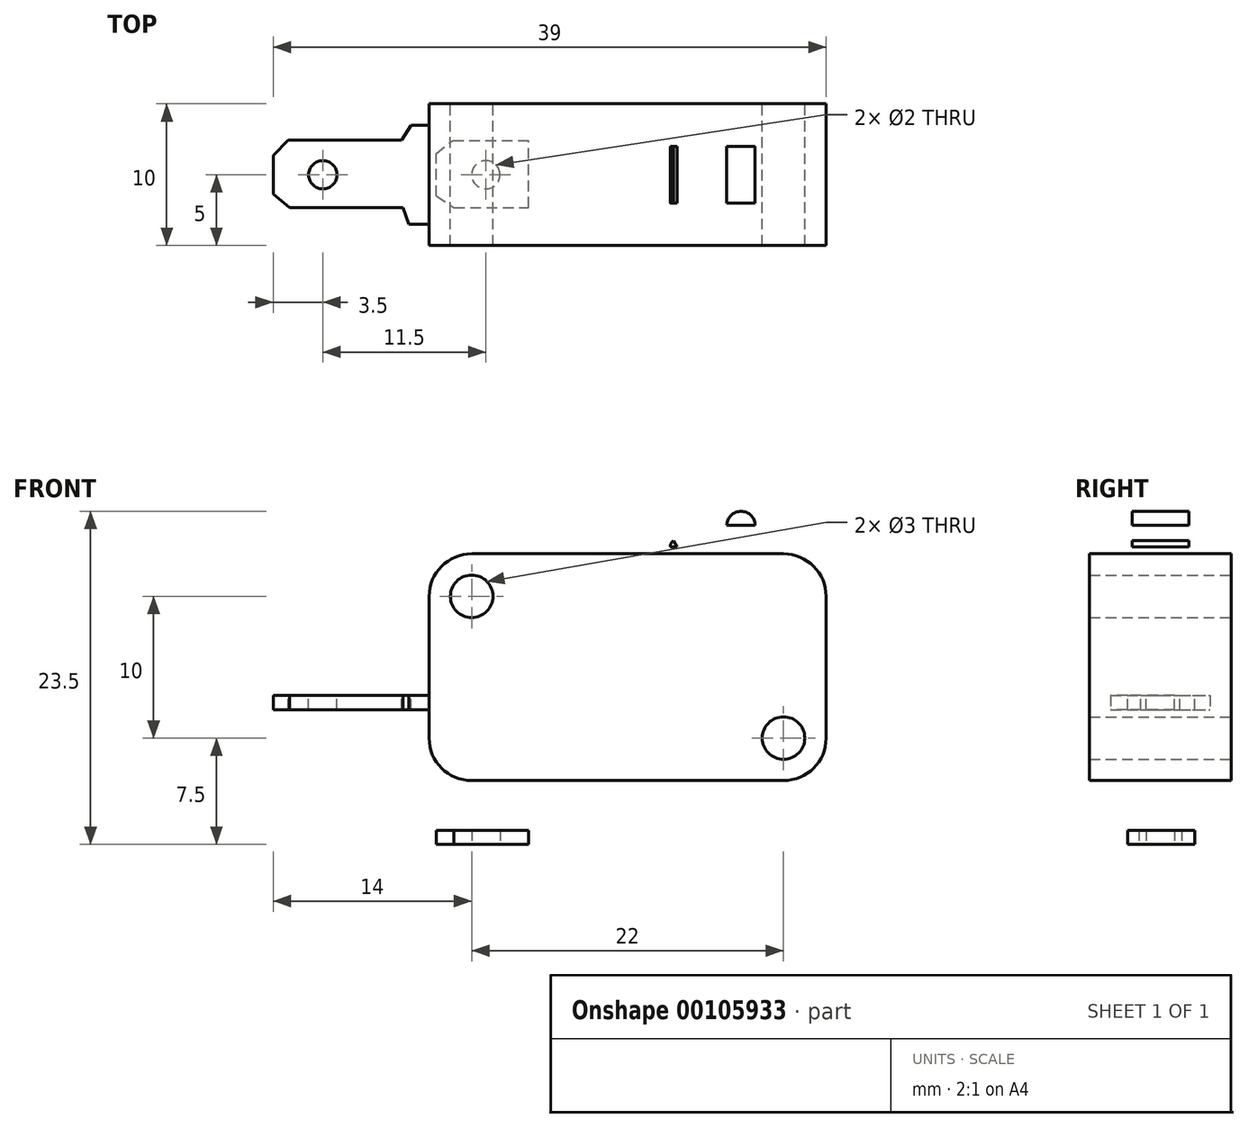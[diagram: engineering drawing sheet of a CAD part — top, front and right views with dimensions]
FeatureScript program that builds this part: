
annotation { "Feature Type Name" : "Feature", "Feature Type Description" : "" }
export const myFeature = defineFeature(function(context is Context, id is Id, definition is map)
    precondition{}
    {
        {
            var Q0;
            Q0=qCreatedBy(makeId("Front.planeOp"),FACE);
            var sketch = newSketch(context, id + "F0", { "sketchPlane" : qUnion([Q0])});
            skLineSegment(sketch, "E0.bottom", {"start": v(11, 8) * mm, "end": v(-11, 8) * mm});
            skLineSegment(sketch, "E0.top", {"start": v(11, -8) * mm, "end": v(-11, -8) * mm});
            skLineSegment(sketch, "E0.left", {"start": v(14, 5) * mm, "end": v(14, -5) * mm});
            skLineSegment(sketch, "E0.right", {"start": v(-14, 5) * mm, "end": v(-14, -5) * mm});
            skPoint(sketch, "E0.middle", {"position": v(0, 0) * mm});
            skPoint(sketch, "E1.visualSharp", {"position": v(-14, -8) * mm});
            skArc(sketch, "E1.filletArc", {"start": v(-14, -5) * mm, "mid": v(-13.12, -7.12) * mm, "end": v(-11, -8) * mm});
            skPoint(sketch, "E2.visualSharp", {"position": v(-14, 8) * mm});
            skArc(sketch, "E2.filletArc", {"start": v(-11, 8) * mm, "mid": v(-13.12, 7.12) * mm, "end": v(-14, 5) * mm});
            skPoint(sketch, "E3.visualSharp", {"position": v(14, 8) * mm});
            skArc(sketch, "E3.filletArc", {"start": v(14, 5) * mm, "mid": v(13.12, 7.12) * mm, "end": v(11, 8) * mm});
            skPoint(sketch, "E4.visualSharp", {"position": v(14, -8) * mm});
            skArc(sketch, "E4.filletArc", {"start": v(11, -8) * mm, "mid": v(13.12, -7.12) * mm, "end": v(14, -5) * mm});
            skCircle(sketch, "E5", {"center": v(-11, 5) * mm, "radius": 1.5 * mm});
            skCircle(sketch, "E6", {"center": v(11, -5) * mm, "radius": 1.5 * mm});
            skLineSegment(sketch, "E7.bottom", {"start": v(7, 8) * mm, "end": v(9, 8) * mm});
            skLineSegment(sketch, "E7.top", {"start": v(7, 10) * mm, "end": v(9, 10) * mm});
            skLineSegment(sketch, "E7.left", {"start": v(7, 8) * mm, "end": v(7, 10) * mm});
            skLineSegment(sketch, "E7.right", {"start": v(9, 8) * mm, "end": v(9, 10) * mm});
            skArc(sketch, "E8", {"start": v(9, 10) * mm, "mid": v(8, 11) * mm, "end": v(7, 10) * mm});
            skLineSegment(sketch, "E9.bottom", {"start": v(3, 8) * mm, "end": v(3.5, 8) * mm});
            skLineSegment(sketch, "E9.top", {"start": v(3, 8.5) * mm, "end": v(3.5, 8.5) * mm});
            skLineSegment(sketch, "E9.left", {"start": v(3, 8) * mm, "end": v(3, 8.5) * mm});
            skLineSegment(sketch, "E9.right", {"start": v(3.5, 8) * mm, "end": v(3.5, 8.46) * mm});
            skLineSegment(sketch, "E10", {"start": v(3.53, 8.52) * mm, "end": v(46.53, 33.96) * mm});
            skLineSegment(sketch, "E11", {"start": v(3.5, 8.5) * mm, "end": v(3.25, 8.93) * mm});
            skLineSegment(sketch, "E12", {"start": v(3.25, 8.93) * mm, "end": v(46.28, 34.39) * mm});
            skLineSegment(sketch, "E13", {"start": v(46.28, 34.39) * mm, "end": v(46.53, 33.96) * mm});
            skArc(sketch, "E14", {"start": v(3.25, 8.93) * mm, "mid": v(3.07, 8.75) * mm, "end": v(3, 8.5) * mm});
            skArc(sketch, "E15.filletArc", {"start": v(3.53, 8.52) * mm, "mid": v(3.5, 8.5) * mm, "end": v(3.5, 8.46) * mm});
            skLineSegment(sketch, "E16.bottom", {"start": v(-14, -2) * mm, "end": v(-25, -2) * mm});
            skLineSegment(sketch, "E16.top", {"start": v(-14, -3) * mm, "end": v(-25, -3) * mm});
            skLineSegment(sketch, "E16.left", {"start": v(-14, -2) * mm, "end": v(-14, -3) * mm});
            skLineSegment(sketch, "E16.right", {"start": v(-25, -2) * mm, "end": v(-25, -3) * mm});
            skLineSegment(sketch, "E17.bottom", {"start": v(-7, -8) * mm, "end": v(-1, -8) * mm});
            skLineSegment(sketch, "E17.top", {"start": v(-7, -12.5) * mm, "end": v(-3.5, -12.5) * mm});
            skLineSegment(sketch, "E17.left", {"start": v(-7, -8) * mm, "end": v(-7, -12.5) * mm});
            skLineSegment(sketch, "E17.right", {"start": v(-1, -8) * mm, "end": v(-1, -10) * mm});
            skLineSegment(sketch, "E18.bottom", {"start": v(-7, -12.5) * mm, "end": v(-13.5, -12.5) * mm});
            skLineSegment(sketch, "E18.top", {"start": v(-7, -11.5) * mm, "end": v(-13.5, -11.5) * mm});
            skLineSegment(sketch, "E18.left", {"start": v(-7, -12.5) * mm, "end": v(-7, -11.5) * mm});
            skLineSegment(sketch, "E18.right", {"start": v(-13.5, -12.5) * mm, "end": v(-13.5, -11.5) * mm});
            skLineSegment(sketch, "E19.bottom", {"start": v(-7, -11.5) * mm, "end": v(-3.5, -11.5) * mm});
            skLineSegment(sketch, "E19.top", {"start": v(-7, -8) * mm, "end": v(-2, -8) * mm});
            skLineSegment(sketch, "E19.left", {"start": v(-7, -11.5) * mm, "end": v(-7, -8) * mm});
            skLineSegment(sketch, "E19.right", {"start": v(-2, -10) * mm, "end": v(-2, -8) * mm});
            skPoint(sketch, "E20.visualSharp", {"position": v(-2, -11.5) * mm});
            skArc(sketch, "E20.filletArc", {"start": v(-3.5, -11.5) * mm, "mid": v(-2.44, -11.06) * mm, "end": v(-2, -10) * mm});
            skPoint(sketch, "E21.visualSharp", {"position": v(-1, -12.5) * mm});
            skArc(sketch, "E21.filletArc", {"start": v(-3.5, -12.5) * mm, "mid": v(-1.73, -11.77) * mm, "end": v(-1, -10) * mm});
            skSolve(sketch);
        }
        {
            var Q0;
            Q0=makeQuery(id+"F0.imprint","IMPRINT",FACE,{"disambiguationData":[TD([[makeQuery(id+"F0.imprint","IMPRINT",EDGE,{"derivedFrom":sQuery(id+"F0.wireOp",EDGE,"E0.left")}),-1.0]])]});
            extrude(context, id + "F1", {"entities" : qUnion([Q0]), "endBound" : BoundingType.SYMMETRIC, "depth" : 10 * mm});
        }
        {
            var Q0;
            Q0=makeQuery(id+"F0.imprint","IMPRINT",FACE,{"disambiguationData":[TD([[makeQuery(id+"F0.imprint","IMPRINT",EDGE,{"derivedFrom":sQuery(id+"F0.wireOp",EDGE,"E18.bottom")}),-1.0]])]});
            var Q1;
            Q1=makeQuery(id+"F0.imprint","IMPRINT",FACE,{"disambiguationData":[TD([[makeQuery(id+"F0.imprint","IMPRINT",EDGE,{"derivedFrom":sQuery(id+"F0.wireOp",EDGE,"E17.bottom")}),-1.0]])]});
            var Q2;
            Q2=makeQuery(id+"F0.imprint","IMPRINT",FACE,{"disambiguationData":[TD([[makeQuery(id+"F0.imprint","IMPRINT",EDGE,{"derivedFrom":sQuery(id+"F0.wireOp",EDGE,"E16.bottom")}),1.0]])]});
            extrude(context, id + "F2", {"entities" : qUnion([Q0, Q1, Q2]), "endBound" : BoundingType.SYMMETRIC, "depth" : 7 * mm});
        }
        {
            var Q0;
            Q0=makeQuery(id+"F0.imprint","IMPRINT",FACE,{"disambiguationData":[TD([[makeQuery(id+"F0.imprint","IMPRINT",EDGE,{"derivedFrom":sQuery(id+"F0.wireOp",EDGE,"E7.bottom")}),1.0]])]});
            var Q1;
            {var subQ0=sQuery(id+"F0.wireOp",EDGE,"E7.top");Q1=makeQuery(id+"F0.imprint","IMPRINT",FACE,{"disambiguationData":[TD([[makeQuery(id+"F0.imprint","IMPRINT",EDGE,{"derivedFrom":subQ0}),1.0]])]});}
            var Q2;
            Q2=makeQuery(id+"F0.imprint","IMPRINT",FACE,{"disambiguationData":[TD([[makeQuery(id+"F0.imprint","IMPRINT",EDGE,{"derivedFrom":sQuery(id+"F0.wireOp",EDGE,"E9.bottom")}),1.0]])]});
            var Q3;
            Q3=makeQuery(id+"F0.imprint","IMPRINT",FACE,{"disambiguationData":[TD([[makeQuery(id+"F0.imprint","IMPRINT",EDGE,{"derivedFrom":sQuery(id+"F0.wireOp",EDGE,"E9.top")}),1.0]])]});
            extrude(context, id + "F3", {"entities" : qUnion([Q0, Q1, Q2, Q3]), "endBound" : BoundingType.SYMMETRIC, "depth" : 4 * mm});
        }
        {
            var Q0;
            Q0=makeQuery(id+"F2.opExtrude","SWEPT_FACE",FACE,{"disambiguationData":[OSD([sQuery(id+"F0.wireOp",EDGE,"E17.top"),sQuery(id+"F0.wireOp",EDGE,"E18.bottom")])]});
            var sketch = newSketch(context, id + "F4", { "sketchPlane" : qUnion([Q0])});
            skCircle(sketch, "E22", {"center": v(-10, 0) * mm, "radius": 1 * mm});
            skLineSegment(sketch, "E23", {"start": v(-13.5, 0) * mm, "end": v(-11, 0) * mm});
            skLineSegment(sketch, "E24", {"start": v(-13.5, -1.5) * mm, "end": v(-13.5, 1.5) * mm});
            skLineSegment(sketch, "E25", {"start": v(-13.5, -1.5) * mm, "end": v(-12.32, -2.43) * mm});
            skLineSegment(sketch, "E26", {"start": v(-13.5, 1.5) * mm, "end": v(-12.24, 2.32) * mm});
            skLineSegment(sketch, "E27", {"start": v(-12.24, 2.32) * mm, "end": v(-5.4, 2.32) * mm});
            skLineSegment(sketch, "E28", {"start": v(-5.4, 2.32) * mm, "end": v(-4.85, 3.5) * mm});
            skLineSegment(sketch, "E29", {"start": v(-12.32, -2.43) * mm, "end": v(-5.47, -2.43) * mm});
            skLineSegment(sketch, "E30", {"start": v(-5.47, -2.43) * mm, "end": v(-4.74, -3.5) * mm});
            skSolve(sketch);
        }
        {
            var Q0;
            {var subQ5=sQuery(id+"F4.wireOp",EDGE,"E26");Q0=makeQuery(id+"F4.imprint","IMPRINT",FACE,{"disambiguationData":[TD([[makeQuery(id+"F4.imprint","IMPRINT",EDGE,{"derivedFrom":subQ5}),1.0]])]});}
            var Q1;
            Q1=makeQuery(id+"F4.imprint","IMPRINT",FACE,{"disambiguationData":[TD([[makeQuery(id+"F4.imprint","IMPRINT",EDGE,{"derivedFrom":sQuery(id+"F4.wireOp",EDGE,"E22")}),1.0]])]});
            var Q2;
            {var subQ4=sQuery(id+"F4.wireOp",EDGE,"E25");Q2=makeQuery(id+"F4.imprint","IMPRINT",FACE,{"disambiguationData":[TD([[makeQuery(id+"F4.imprint","IMPRINT",EDGE,{"derivedFrom":subQ4}),-1.0]])]});}
            extrude(context, id + "F5", {"entities" : qUnion([Q0, Q1, Q2]), "operationType" : NewBodyOperationType.REMOVE, "oppositeDirection" : true, "depth" : 1 * mm});
        }
        {
            var Q0;
            Q0=makeQuery(id+"F2.opExtrude","SWEPT_FACE",FACE,{"disambiguationData":[OSD([sQuery(id+"F0.wireOp",EDGE,"E16.bottom")])]});
            var sketch = newSketch(context, id + "F6", { "sketchPlane" : qUnion([Q0])});
            skLineSegment(sketch, "E31", {"start": v(-25, 1.38) * mm, "end": v(-25, -1.38) * mm});
            skLineSegment(sketch, "E32", {"start": v(-25, 1.37) * mm, "end": v(-23.94, 2.43) * mm});
            skLineSegment(sketch, "E33", {"start": v(-23.94, 2.43) * mm, "end": v(-15.94, 2.43) * mm});
            skLineSegment(sketch, "E34", {"start": v(-15.94, 2.43) * mm, "end": v(-15.29, 3.5) * mm});
            skLineSegment(sketch, "E35", {"start": v(-25, -1.37) * mm, "end": v(-23.83, -2.32) * mm});
            skLineSegment(sketch, "E36", {"start": v(-23.83, -2.32) * mm, "end": v(-15.83, -2.32) * mm});
            skLineSegment(sketch, "E37", {"start": v(-15.83, -2.32) * mm, "end": v(-15.42, -3.5) * mm});
            skCircle(sketch, "E38", {"center": v(-21.5, 0) * mm, "radius": 1 * mm});
            skLineSegment(sketch, "E39", {"start": v(-22.5, 0) * mm, "end": v(-25, 0) * mm});
            skLineSegment(sketch, "E40", {"start": v(-25, 0) * mm, "end": v(-22.5, 0) * mm});
            skLineSegment(sketch, "E41", {"start": v(-15.29, 3.5) * mm, "end": v(-25, 3.5) * mm});
            skLineSegment(sketch, "E42", {"start": v(-25, 3.5) * mm, "end": v(-25, 1.38) * mm});
            skLineSegment(sketch, "E43", {"start": v(-25, -1.38) * mm, "end": v(-25, -3.5) * mm});
            skLineSegment(sketch, "E44", {"start": v(-25, -3.5) * mm, "end": v(-15.42, -3.5) * mm});
            skSolve(sketch);
        }
        {
            var Q0;
            Q0=makeQuery(id+"F6.imprint","IMPRINT",FACE,{"disambiguationData":[TD([[makeQuery(id+"F6.imprint","IMPRINT",EDGE,{"derivedFrom":sQuery(id+"F6.wireOp",EDGE,"E32")}),1.0]])]});
            var Q1;
            Q1=makeQuery(id+"F6.imprint","IMPRINT",FACE,{"disambiguationData":[TD([[makeQuery(id+"F6.imprint","IMPRINT",EDGE,{"derivedFrom":sQuery(id+"F6.wireOp",EDGE,"E35")}),-1.0]])]});
            var Q2;
            Q2=makeQuery(id+"F6.imprint","IMPRINT",FACE,{"disambiguationData":[TD([[makeQuery(id+"F6.imprint","IMPRINT",EDGE,{"derivedFrom":sQuery(id+"F6.wireOp",EDGE,"E38")}),1.0]])]});
            extrude(context, id + "F7", {"entities" : qUnion([Q0, Q1, Q2]), "operationType" : NewBodyOperationType.REMOVE, "oppositeDirection" : true, "depth" : 1 * mm});
        }
    });
